# Revit family: Commercial_Water Dispenser-Elkay-EBWDCM0SSC-BD
name_source: partatom
category: Plumbing Fixtures
units: mm (PartAtom-declared; Revit-internal decimal feet)

## family parameters
Cut with Voids When Loaded = No
Host = Face
Maintain Annotation Orientation = No
OmniClass Number = 23.65.70.14.11
OmniClass Title = Drinking Fountains/Coolers
Part Type = Normal
Room Calculation Point = No
Round Connector Dimension = Use Diameter
Shared = No

## types (1)
- EBWDCM0SSC-BD (Commercial Water Dispenser Non-Filtered Non-Refrigerated Stainless)
    Activation Method = Mechanical Bottle Filler Button
    Approx. Shipping Weight (lbs) = 26
    Assembly Code = D2010800
    Default Elevation = 48 "
    Description = Elkay ezH2O Commercial Water Dispenser Non-Filtered Non Refrigerated Stainless with brass drain
    Height = 28 "
    Inlet connection = 2 "
    Length = 5.13 "
    Main Material = Finish-Elkay-Stainless Steel
    Manufacturer = Elkay Manufacturer Company
    Manufacturer Brand = Elkay (by Zurn Elkay Water Solutions)
    Model = EBWDCM0SSC-BD
    Outlet connection = 2 "
    Product Documentation Link = https://www.elkayfiles.com
    Product Installation Sheet URL = https://www.elkayfiles.com
    Product Page URL = https://www.elkay.com
    Product Weight (lbs) = 25
    Repair Parts URL = https://www.elkayfiles.com
    Second material = Elkay-Transparent
    URL = https://www.elkay.com
    Width = 18 "

## geometry (parser evidence)
native form markers: Sweep x5
no freeform markers — native parametric forms only
